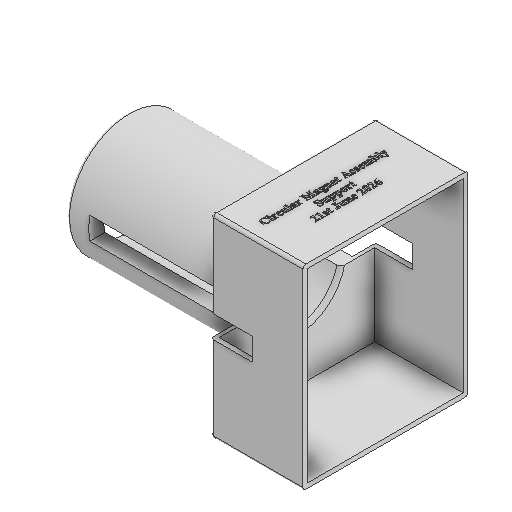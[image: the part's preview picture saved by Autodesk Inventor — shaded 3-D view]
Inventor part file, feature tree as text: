
AUTODESK INVENTOR PART (.ipt)
format: ipt  version: 2025 (Build 290162000, 162)  size: 1,741,824 bytes
history: native  units: in
note: dims shown in document units (in); Inventor stores cm internally (conversion verified against a paired STEP export)
features: sketch x9, extrude x8, fillet x4, emboss x1
ambient origin geometry x8: Origin, YZ Plane, XZ Plane, XY Plane, X Axis, Y Axis, Z Axis, Center Point
bodies: Solid1 (feature_tree)
feature tree (22):
  extrude  "Extrusion1"  Depth=7.0in TaperAngle=0.0deg
  extrude  "Extrusion2"  Depth=7.874in TaperAngle=0.0deg
  extrude  "Extrusion3"  Depth=5.8155in TaperAngle=0.0deg
  extrude  "Extrusion4"  Depth=5.5in
  extrude  "Extrusion5"  Depth=0.1575in
  extrude  "Extrusion7"  Depth=2.9528in TaperAngle=0.0deg
  emboss  "Emboss1"
  extrude  "Extrusion8"  Depth=0.75in
  fillet  "Fillet1"  Radius=7.874in
  fillet  "Fillet2"  Radius=1.378in
  extrude  "Extrusion9"  TaperAngle=0.0deg  [1 undecoded]
  fillet  "Fillet3"  Radius=0.1in
  fillet  "Fillet4"  Radius=0.1in
  sketch  "Sketch1"  dims[d0=4.0in d1=7.0in d2=0.0in]
  sketch  "Sketch2"  dims[d3=3.02in d4=7.874in d5=0.0in]
  sketch  "Sketch4"  dims[d6=0.75in d7=5.8155in d8=0.0in]
  sketch  "Sketch5"  dims[d9=6.5in d10=5.5in]
  sketch  "Sketch6"  dims[d11=3.0709in d12=0.0in d13=0.1575in]
  sketch  "Sketch10"  dims[d14=0.1575in d15=2.9528in d16=0.0in]
  sketch  "Sketch13"  dims[d19=4.8125in d20=0.0in d21=7.874in d22=0.75in d23=7.874in d24=1.378in d25=0.0in]
  sketch  "Sketch14"  dims[d26=0.0787in d27=0.0in d28=0.0in d29=0.0in d30=0.1in d31=0.1in]
  sketch  "Sketch15"  dims[d32=0.0in d33=0.0in d34=0.1in d35=3.02in d36=0.125in]
note: 1 required parameter value undecoded (feature->parameter linkage not recoverable at this tier; creation-order binding heuristic only, values carry confidence <= 0.55)
